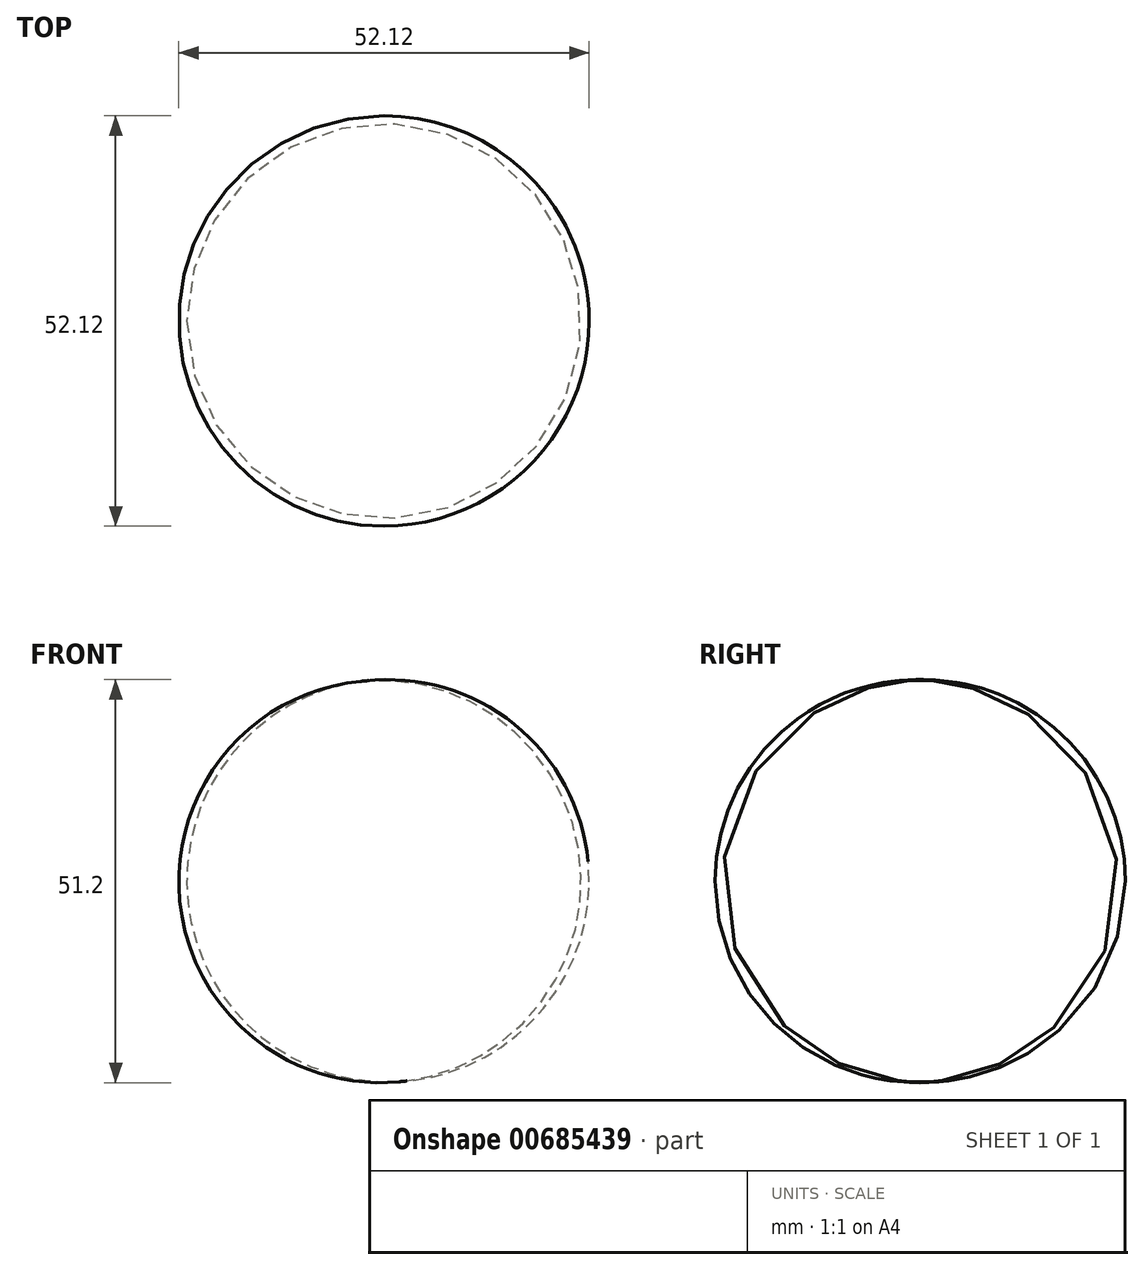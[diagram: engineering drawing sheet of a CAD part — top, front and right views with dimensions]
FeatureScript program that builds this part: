
annotation { "Feature Type Name" : "Feature", "Feature Type Description" : "" }
export const myFeature = defineFeature(function(context is Context, id is Id, definition is map)
    precondition{}
    {
        {
            var Q0;
            Q0=qCreatedBy(makeId("Front.planeOp"),FACE);
            var sketch = newSketch(context, id + "F0", { "sketchPlane" : qUnion([Q0])});
            skArc(sketch, "E0", {"start": v(-28.64, 0) * mm, "mid": v(-6.15, 27.82) * mm, "end": v(-33.52, 50.86) * mm});
            skLineSegment(sketch, "E1", {"start": v(-33.52, 50.86) * mm, "end": v(-28.64, 0) * mm});
            skSolve(sketch);
        }
        {
            var Q0;
            Q0=makeQuery(id+"F0.imprint","IMPRINT",FACE,{"disambiguationData":[TD([[makeQuery(id+"F0.imprint","IMPRINT",EDGE,{"derivedFrom":sQuery(id+"F0.wireOp",EDGE,"E0")}),1.0]])]});
            var Q1;
            Q1=sQuery(id+"F0.wireOp",EDGE,"E1");
            revolve(context, id + "F1", {"entities" : qUnion([Q0]), "axis" : qUnion([Q1]), "revolveType" : RevolveType.FULL});
        }
    });
